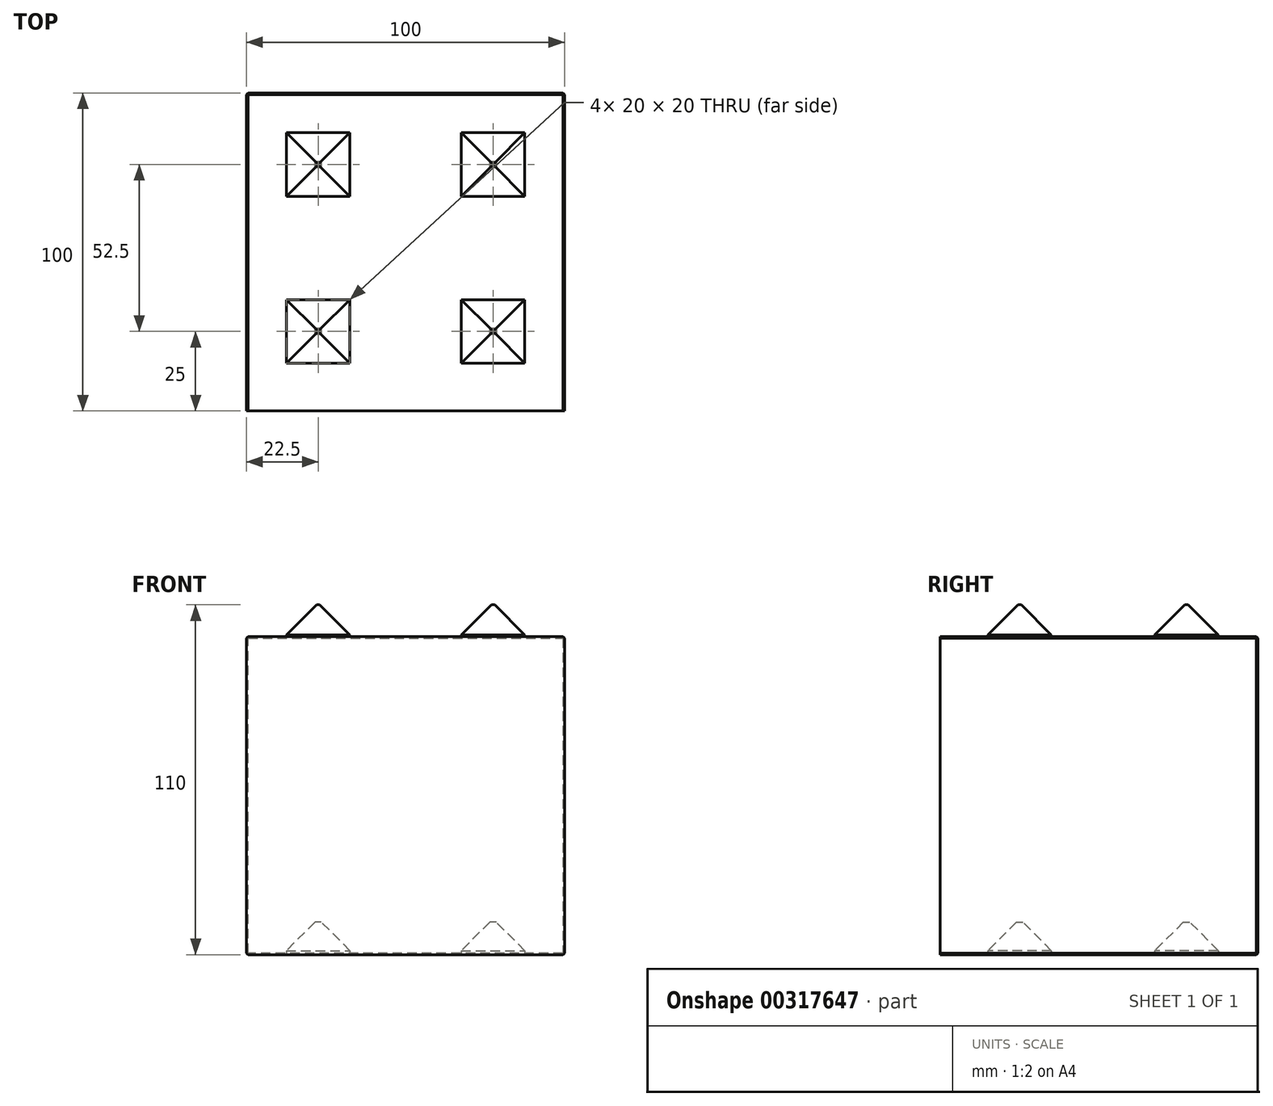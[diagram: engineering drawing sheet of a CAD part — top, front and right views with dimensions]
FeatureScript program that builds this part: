
annotation { "Feature Type Name" : "Feature", "Feature Type Description" : "" }
export const myFeature = defineFeature(function(context is Context, id is Id, definition is map)
    precondition{}
    {
        {
            var Q0;
            Q0=qCreatedBy(makeId("Front.planeOp"),FACE);
            var sketch = newSketch(context, id + "F0", { "sketchPlane" : qUnion([Q0])});
            skLineSegment(sketch, "E0.bottom", {"start": v(-50, 50) * mm, "end": v(50, 50) * mm});
            skLineSegment(sketch, "E0.top", {"start": v(-50, -50) * mm, "end": v(50, -50) * mm});
            skLineSegment(sketch, "E0.left", {"start": v(-50, 50) * mm, "end": v(-50, -50) * mm});
            skLineSegment(sketch, "E0.right", {"start": v(50, 50) * mm, "end": v(50, -50) * mm});
            skSolve(sketch);
        }
        {
            var Q0;
            Q0 = qSketchRegion(id + "F0", true);
            extrude(context, id + "F1", {"entities" : qUnion([Q0]), "endBound" : BoundingType.SYMMETRIC, "depth" : 200 * mm});
        }
        {
            var Q0;
            Q0=makeQuery(id+"F1.opExtrude","SWEPT_FACE",FACE,{"disambiguationData":[OSD([sQuery(id+"F0.wireOp",EDGE,"E0.bottom")])]});
            var sketch = newSketch(context, id + "F2", { "sketchPlane" : qUnion([Q0])});
            skLineSegment(sketch, "E1", {"start": v(-37.5, 87.5) * mm, "end": v(-37.5, 67.5) * mm});
            skLineSegment(sketch, "E2", {"start": v(-17.5, 87.5) * mm, "end": v(-17.5, 67.5) * mm});
            skLineSegment(sketch, "E3", {"start": v(17.5, 87.5) * mm, "end": v(17.5, 67.5) * mm});
            skLineSegment(sketch, "E4", {"start": v(37.5, 87.5) * mm, "end": v(37.5, 67.5) * mm});
            skLineSegment(sketch, "E5", {"start": v(-37.5, 87.5) * mm, "end": v(-17.5, 87.5) * mm});
            skLineSegment(sketch, "E6", {"start": v(-37.5, 67.5) * mm, "end": v(-17.5, 67.5) * mm});
            skLineSegment(sketch, "E7", {"start": v(-37.5, 35) * mm, "end": v(-17.5, 35) * mm});
            skLineSegment(sketch, "E8", {"start": v(-37.5, 15) * mm, "end": v(-17.5, 15) * mm});
            skLineSegment(sketch, "E9", {"start": v(-37.5, -15) * mm, "end": v(-17.5, -15) * mm});
            skLineSegment(sketch, "E10", {"start": v(-37.5, -35) * mm, "end": v(-17.5, -35) * mm});
            skLineSegment(sketch, "E11", {"start": v(-37.5, -67.5) * mm, "end": v(-17.5, -67.5) * mm});
            skLineSegment(sketch, "E12", {"start": v(-37.5, -87.5) * mm, "end": v(-17.5, -87.5) * mm});
            skLineSegment(sketch, "E13.trimOffspring", {"start": v(-37.5, -67.5) * mm, "end": v(-37.5, -87.5) * mm});
            skLineSegment(sketch, "E14.trimOffspring", {"start": v(-17.5, -67.5) * mm, "end": v(-17.5, -87.5) * mm});
            skLineSegment(sketch, "E15.trimOffspring", {"start": v(17.5, -67.5) * mm, "end": v(17.5, -87.5) * mm});
            skLineSegment(sketch, "E16.trimOffspring", {"start": v(37.5, -67.5) * mm, "end": v(37.5, -87.5) * mm});
            skLineSegment(sketch, "E17.trimOffspring", {"start": v(17.5, -67.5) * mm, "end": v(37.5, -67.5) * mm});
            skLineSegment(sketch, "E18.trimOffspring", {"start": v(17.5, -87.5) * mm, "end": v(37.5, -87.5) * mm});
            skLineSegment(sketch, "E19.trimOffspring", {"start": v(17.5, -15) * mm, "end": v(37.5, -15) * mm});
            skLineSegment(sketch, "E20.trimOffspring", {"start": v(17.5, -35) * mm, "end": v(37.5, -35) * mm});
            skLineSegment(sketch, "E21.trimOffspring", {"start": v(17.5, 15) * mm, "end": v(37.5, 15) * mm});
            skLineSegment(sketch, "E22.trimOffspring", {"start": v(17.5, 35) * mm, "end": v(37.5, 35) * mm});
            skLineSegment(sketch, "E23.trimOffspring", {"start": v(17.5, 67.5) * mm, "end": v(37.5, 67.5) * mm});
            skLineSegment(sketch, "E24.trimOffspring", {"start": v(17.5, 87.5) * mm, "end": v(37.5, 87.5) * mm});
            skLineSegment(sketch, "E25.trimOffspring", {"start": v(-37.5, 35) * mm, "end": v(-37.5, 15) * mm});
            skLineSegment(sketch, "E26.trimOffspring", {"start": v(-17.5, 35) * mm, "end": v(-17.5, 15) * mm});
            skLineSegment(sketch, "E27.trimOffspring", {"start": v(17.5, 35) * mm, "end": v(17.5, 15) * mm});
            skLineSegment(sketch, "E28.trimOffspring", {"start": v(37.5, 35) * mm, "end": v(37.5, 15) * mm});
            skLineSegment(sketch, "E29.trimOffspring", {"start": v(-37.5, -15) * mm, "end": v(-37.5, -35) * mm});
            skLineSegment(sketch, "E30.trimOffspring", {"start": v(-17.5, -15) * mm, "end": v(-17.5, -35) * mm});
            skLineSegment(sketch, "E31.trimOffspring", {"start": v(17.5, -15) * mm, "end": v(17.5, -35) * mm});
            skLineSegment(sketch, "E32.trimOffspring", {"start": v(37.5, -15) * mm, "end": v(37.5, -35) * mm});
            skSolve(sketch);
        }
        {
            var Q0;
            Q0 = qSketchRegion(id + "F2", true);
            extrude(context, id + "F3", {"entities" : qUnion([Q0]), "operationType" : NewBodyOperationType.ADD, "depth" : 10 * mm});
        }
        {
            var Q0;
            Q0=makeQuery(id+"F3.opExtrude","CAP_FACE",FACE,{"disambiguationData":[OSD([sQuery(id+"F2.wireOp",EDGE,"E15.trimOffspring"),sQuery(id+"F2.wireOp",EDGE,"E16.trimOffspring"),sQuery(id+"F2.wireOp",EDGE,"E17.trimOffspring"),sQuery(id+"F2.wireOp",EDGE,"E18.trimOffspring")])],"isStart":false});
            var Q1;
            Q1=makeQuery(id+"F3.opExtrude","CAP_FACE",FACE,{"disambiguationData":[OSD([sQuery(id+"F2.wireOp",EDGE,"E19.trimOffspring"),sQuery(id+"F2.wireOp",EDGE,"E20.trimOffspring"),sQuery(id+"F2.wireOp",EDGE,"E31.trimOffspring"),sQuery(id+"F2.wireOp",EDGE,"E32.trimOffspring")])],"isStart":false});
            var Q2;
            Q2=makeQuery(id+"F3.opExtrude","CAP_FACE",FACE,{"disambiguationData":[OSD([sQuery(id+"F2.wireOp",EDGE,"E11"),sQuery(id+"F2.wireOp",EDGE,"E12"),sQuery(id+"F2.wireOp",EDGE,"E13.trimOffspring"),sQuery(id+"F2.wireOp",EDGE,"E14.trimOffspring")])],"isStart":false});
            var Q3;
            Q3=makeQuery(id+"F3.opExtrude","CAP_FACE",FACE,{"disambiguationData":[OSD([sQuery(id+"F2.wireOp",EDGE,"E9"),sQuery(id+"F2.wireOp",EDGE,"E10"),sQuery(id+"F2.wireOp",EDGE,"E29.trimOffspring"),sQuery(id+"F2.wireOp",EDGE,"E30.trimOffspring")])],"isStart":false});
            var Q4;
            Q4=makeQuery(id+"F3.opExtrude","CAP_FACE",FACE,{"disambiguationData":[OSD([sQuery(id+"F2.wireOp",EDGE,"E7"),sQuery(id+"F2.wireOp",EDGE,"E8"),sQuery(id+"F2.wireOp",EDGE,"E25.trimOffspring"),sQuery(id+"F2.wireOp",EDGE,"E26.trimOffspring")])],"isStart":false});
            var Q5;
            Q5=makeQuery(id+"F3.opExtrude","CAP_FACE",FACE,{"disambiguationData":[OSD([sQuery(id+"F2.wireOp",EDGE,"E1"),sQuery(id+"F2.wireOp",EDGE,"E2"),sQuery(id+"F2.wireOp",EDGE,"E5"),sQuery(id+"F2.wireOp",EDGE,"E6")])],"isStart":false});
            var Q6;
            Q6=makeQuery(id+"F3.opExtrude","CAP_FACE",FACE,{"disambiguationData":[OSD([sQuery(id+"F2.wireOp",EDGE,"E3"),sQuery(id+"F2.wireOp",EDGE,"E4"),sQuery(id+"F2.wireOp",EDGE,"E23.trimOffspring"),sQuery(id+"F2.wireOp",EDGE,"E24.trimOffspring")])],"isStart":false});
            var Q7;
            Q7=makeQuery(id+"F3.opExtrude","CAP_FACE",FACE,{"disambiguationData":[OSD([sQuery(id+"F2.wireOp",EDGE,"E21.trimOffspring"),sQuery(id+"F2.wireOp",EDGE,"E22.trimOffspring"),sQuery(id+"F2.wireOp",EDGE,"E27.trimOffspring"),sQuery(id+"F2.wireOp",EDGE,"E28.trimOffspring")])],"isStart":false});
            chamfer(context, id + "F4", {"entities" : qUnion([Q0, Q1, Q2, Q3, Q4, Q5, Q6, Q7]), "width" : 9.5 * mm, "tangentPropagation" : true});
        }
        {
            var Q0;
            Q0=makeQuery(id+"F1.opExtrude","SWEPT_FACE",FACE,{"disambiguationData":[OSD([sQuery(id+"F0.wireOp",EDGE,"E0.top")])]});
            var sketch = newSketch(context, id + "F5", { "sketchPlane" : qUnion([Q0])});
            skLineSegment(sketch, "E33", {"start": v(-37.5, 87.5) * mm, "end": v(-37.5, 67.5) * mm});
            skLineSegment(sketch, "E34", {"start": v(-17.5, 87.5) * mm, "end": v(-17.5, 67.5) * mm});
            skLineSegment(sketch, "E35", {"start": v(17.5, 87.5) * mm, "end": v(17.5, 67.5) * mm});
            skLineSegment(sketch, "E36", {"start": v(37.5, 87.5) * mm, "end": v(37.5, 67.5) * mm});
            skLineSegment(sketch, "E37", {"start": v(-37.5, 87.5) * mm, "end": v(-17.5, 87.5) * mm});
            skLineSegment(sketch, "E38", {"start": v(-37.5, 67.5) * mm, "end": v(-17.5, 67.5) * mm});
            skLineSegment(sketch, "E39", {"start": v(-37.5, 35) * mm, "end": v(-17.5, 35) * mm});
            skLineSegment(sketch, "E40", {"start": v(-37.5, 15) * mm, "end": v(-17.5, 15) * mm});
            skLineSegment(sketch, "E41", {"start": v(-37.5, -15) * mm, "end": v(-17.5, -15) * mm});
            skLineSegment(sketch, "E42", {"start": v(-37.5, -35) * mm, "end": v(-17.5, -35) * mm});
            skLineSegment(sketch, "E43", {"start": v(-37.5, -67.5) * mm, "end": v(-17.5, -67.5) * mm});
            skLineSegment(sketch, "E44", {"start": v(-37.5, -87.5) * mm, "end": v(-17.5, -87.5) * mm});
            skLineSegment(sketch, "E45.trimOffspring", {"start": v(-37.5, -67.5) * mm, "end": v(-37.5, -87.5) * mm});
            skLineSegment(sketch, "E46.trimOffspring", {"start": v(-17.5, -67.5) * mm, "end": v(-17.5, -87.5) * mm});
            skLineSegment(sketch, "E47.trimOffspring", {"start": v(17.5, -67.5) * mm, "end": v(17.5, -87.5) * mm});
            skLineSegment(sketch, "E48.trimOffspring", {"start": v(37.5, -67.5) * mm, "end": v(37.5, -87.5) * mm});
            skLineSegment(sketch, "E49.trimOffspring", {"start": v(17.5, -67.5) * mm, "end": v(37.5, -67.5) * mm});
            skLineSegment(sketch, "E50.trimOffspring", {"start": v(17.5, -87.5) * mm, "end": v(37.5, -87.5) * mm});
            skLineSegment(sketch, "E51.trimOffspring", {"start": v(17.5, -15) * mm, "end": v(37.5, -15) * mm});
            skLineSegment(sketch, "E52.trimOffspring", {"start": v(17.5, -35) * mm, "end": v(37.5, -35) * mm});
            skLineSegment(sketch, "E53.trimOffspring", {"start": v(17.5, 15) * mm, "end": v(37.5, 15) * mm});
            skLineSegment(sketch, "E54.trimOffspring", {"start": v(17.5, 35) * mm, "end": v(37.5, 35) * mm});
            skLineSegment(sketch, "E55.trimOffspring", {"start": v(17.5, 67.5) * mm, "end": v(37.5, 67.5) * mm});
            skLineSegment(sketch, "E56.trimOffspring", {"start": v(17.5, 87.5) * mm, "end": v(37.5, 87.5) * mm});
            skLineSegment(sketch, "E57.trimOffspring", {"start": v(-37.5, 35) * mm, "end": v(-37.5, 15) * mm});
            skLineSegment(sketch, "E58.trimOffspring", {"start": v(-17.5, 35) * mm, "end": v(-17.5, 15) * mm});
            skLineSegment(sketch, "E59.trimOffspring", {"start": v(17.5, 35) * mm, "end": v(17.5, 15) * mm});
            skLineSegment(sketch, "E60.trimOffspring", {"start": v(37.5, 35) * mm, "end": v(37.5, 15) * mm});
            skLineSegment(sketch, "E61.trimOffspring", {"start": v(-37.5, -15) * mm, "end": v(-37.5, -35) * mm});
            skLineSegment(sketch, "E62.trimOffspring", {"start": v(-17.5, -15) * mm, "end": v(-17.5, -35) * mm});
            skLineSegment(sketch, "E63.trimOffspring", {"start": v(17.5, -15) * mm, "end": v(17.5, -35) * mm});
            skLineSegment(sketch, "E64.trimOffspring", {"start": v(37.5, -15) * mm, "end": v(37.5, -35) * mm});
            skSolve(sketch);
        }
        {
            var Q0;
            Q0=makeQuery(id+"F5.imprint","IMPRINT",FACE,{"disambiguationData":[TD([[makeQuery(id+"F5.imprint","IMPRINT",EDGE,{"derivedFrom":sQuery(id+"F5.wireOp",EDGE,"E33")}),1.0]])]});
            var Q1;
            Q1=makeQuery(id+"F5.imprint","IMPRINT",FACE,{"disambiguationData":[TD([[makeQuery(id+"F5.imprint","IMPRINT",EDGE,{"derivedFrom":sQuery(id+"F5.wireOp",EDGE,"E35")}),1.0]])]});
            var Q2;
            Q2=makeQuery(id+"F5.imprint","IMPRINT",FACE,{"disambiguationData":[TD([[makeQuery(id+"F5.imprint","IMPRINT",EDGE,{"derivedFrom":sQuery(id+"F5.wireOp",EDGE,"E53.trimOffspring")}),1.0]])]});
            var Q3;
            Q3=makeQuery(id+"F5.imprint","IMPRINT",FACE,{"disambiguationData":[TD([[makeQuery(id+"F5.imprint","IMPRINT",EDGE,{"derivedFrom":sQuery(id+"F5.wireOp",EDGE,"E39")}),-1.0]])]});
            var Q4;
            Q4=makeQuery(id+"F5.imprint","IMPRINT",FACE,{"disambiguationData":[TD([[makeQuery(id+"F5.imprint","IMPRINT",EDGE,{"derivedFrom":sQuery(id+"F5.wireOp",EDGE,"E41")}),-1.0]])]});
            var Q5;
            Q5=makeQuery(id+"F5.imprint","IMPRINT",FACE,{"disambiguationData":[TD([[makeQuery(id+"F5.imprint","IMPRINT",EDGE,{"derivedFrom":sQuery(id+"F5.wireOp",EDGE,"E51.trimOffspring")}),-1.0]])]});
            var Q6;
            Q6=makeQuery(id+"F5.imprint","IMPRINT",FACE,{"disambiguationData":[TD([[makeQuery(id+"F5.imprint","IMPRINT",EDGE,{"derivedFrom":sQuery(id+"F5.wireOp",EDGE,"E47.trimOffspring")}),1.0]])]});
            var Q7;
            Q7=makeQuery(id+"F5.imprint","IMPRINT",FACE,{"disambiguationData":[TD([[makeQuery(id+"F5.imprint","IMPRINT",EDGE,{"derivedFrom":sQuery(id+"F5.wireOp",EDGE,"E43")}),-1.0]])]});
            extrude(context, id + "F6", {"entities" : qUnion([Q0, Q1, Q2, Q3, Q4, Q5, Q6, Q7]), "operationType" : NewBodyOperationType.REMOVE, "oppositeDirection" : true, "depth" : 10.25 * mm});
        }
        {
            var Q0;
            Q0=makeQuery(id+"F6.boolean.opBoolean","COPY",FACE,{"derivedFrom":makeQuery(id+"F6.opExtrude","CAP_FACE",FACE,{"disambiguationData":[OSD([sQuery(id+"F5.wireOp",EDGE,"E35"),sQuery(id+"F5.wireOp",EDGE,"E36"),sQuery(id+"F5.wireOp",EDGE,"E55.trimOffspring"),sQuery(id+"F5.wireOp",EDGE,"E56.trimOffspring")])],"isStart":false})});
            var Q1;
            Q1=makeQuery(id+"F6.boolean.opBoolean","COPY",FACE,{"derivedFrom":makeQuery(id+"F6.opExtrude","CAP_FACE",FACE,{"disambiguationData":[OSD([sQuery(id+"F5.wireOp",EDGE,"E33"),sQuery(id+"F5.wireOp",EDGE,"E34"),sQuery(id+"F5.wireOp",EDGE,"E37"),sQuery(id+"F5.wireOp",EDGE,"E38")])],"isStart":false})});
            var Q2;
            Q2=makeQuery(id+"F6.boolean.opBoolean","COPY",FACE,{"derivedFrom":makeQuery(id+"F6.opExtrude","CAP_FACE",FACE,{"disambiguationData":[OSD([sQuery(id+"F5.wireOp",EDGE,"E39"),sQuery(id+"F5.wireOp",EDGE,"E40"),sQuery(id+"F5.wireOp",EDGE,"E57.trimOffspring"),sQuery(id+"F5.wireOp",EDGE,"E58.trimOffspring")])],"isStart":false})});
            var Q3;
            Q3=makeQuery(id+"F6.boolean.opBoolean","COPY",FACE,{"derivedFrom":makeQuery(id+"F6.opExtrude","CAP_FACE",FACE,{"disambiguationData":[OSD([sQuery(id+"F5.wireOp",EDGE,"E53.trimOffspring"),sQuery(id+"F5.wireOp",EDGE,"E54.trimOffspring"),sQuery(id+"F5.wireOp",EDGE,"E59.trimOffspring"),sQuery(id+"F5.wireOp",EDGE,"E60.trimOffspring")])],"isStart":false})});
            var Q4;
            Q4=makeQuery(id+"F6.boolean.opBoolean","COPY",FACE,{"derivedFrom":makeQuery(id+"F6.opExtrude","CAP_FACE",FACE,{"disambiguationData":[OSD([sQuery(id+"F5.wireOp",EDGE,"E51.trimOffspring"),sQuery(id+"F5.wireOp",EDGE,"E52.trimOffspring"),sQuery(id+"F5.wireOp",EDGE,"E63.trimOffspring"),sQuery(id+"F5.wireOp",EDGE,"E64.trimOffspring")])],"isStart":false})});
            var Q5;
            Q5=makeQuery(id+"F6.boolean.opBoolean","COPY",FACE,{"derivedFrom":makeQuery(id+"F6.opExtrude","CAP_FACE",FACE,{"disambiguationData":[OSD([sQuery(id+"F5.wireOp",EDGE,"E41"),sQuery(id+"F5.wireOp",EDGE,"E42"),sQuery(id+"F5.wireOp",EDGE,"E61.trimOffspring"),sQuery(id+"F5.wireOp",EDGE,"E62.trimOffspring")])],"isStart":false})});
            var Q6;
            Q6=makeQuery(id+"F6.boolean.opBoolean","COPY",FACE,{"derivedFrom":makeQuery(id+"F6.opExtrude","CAP_FACE",FACE,{"disambiguationData":[OSD([sQuery(id+"F5.wireOp",EDGE,"E43"),sQuery(id+"F5.wireOp",EDGE,"E44"),sQuery(id+"F5.wireOp",EDGE,"E45.trimOffspring"),sQuery(id+"F5.wireOp",EDGE,"E46.trimOffspring")])],"isStart":false})});
            var Q7;
            Q7=makeQuery(id+"F6.boolean.opBoolean","COPY",FACE,{"derivedFrom":makeQuery(id+"F6.opExtrude","CAP_FACE",FACE,{"disambiguationData":[OSD([sQuery(id+"F5.wireOp",EDGE,"E47.trimOffspring"),sQuery(id+"F5.wireOp",EDGE,"E48.trimOffspring"),sQuery(id+"F5.wireOp",EDGE,"E49.trimOffspring"),sQuery(id+"F5.wireOp",EDGE,"E50.trimOffspring")])],"isStart":false})});
            chamfer(context, id + "F7", {"entities" : qUnion([Q0, Q1, Q2, Q3, Q4, Q5, Q6, Q7]), "width" : 9 * mm, "tangentPropagation" : true});
        }
        {
            var Q0;
            Q0=makeQuery(id+"F1.opExtrude","CAP_FACE",FACE,{"disambiguationData":[OSD([sQuery(id+"F0.wireOp",EDGE,"E0.bottom"),sQuery(id+"F0.wireOp",EDGE,"E0.top"),sQuery(id+"F0.wireOp",EDGE,"E0.left"),sQuery(id+"F0.wireOp",EDGE,"E0.right")])],"isStart":false});
            var Q1;
            Q1=makeQuery(id+"F1.opExtrude","CAP_FACE",FACE,{"disambiguationData":[OSD([sQuery(id+"F0.wireOp",EDGE,"E0.bottom"),sQuery(id+"F0.wireOp",EDGE,"E0.top"),sQuery(id+"F0.wireOp",EDGE,"E0.left"),sQuery(id+"F0.wireOp",EDGE,"E0.right")])],"isStart":true});
            var Q2;
            Q2=makeQuery(id+"F1.opExtrude","SWEPT_FACE",FACE,{"disambiguationData":[OSD([sQuery(id+"F0.wireOp",EDGE,"E0.right")])]});
            var Q3;
            Q3=makeQuery(id+"F1.opExtrude","SWEPT_FACE",FACE,{"disambiguationData":[OSD([sQuery(id+"F0.wireOp",EDGE,"E0.left")])]});
            chamfer(context, id + "F8", {"entities" : qUnion([Q0, Q1, Q2, Q3]), "width" : .5 * mm, "tangentPropagation" : true});
        }
        {
            var Q0;
            Q0=makeQuery(id+"F1.opExtrude","SWEPT_FACE",FACE,{"disambiguationData":[OSD([sQuery(id+"F0.wireOp",EDGE,"E0.right")])]});
            var sketch = newSketch(context, id + "F9", { "sketchPlane" : qUnion([Q0])});
            skLineSegment(sketch, "E65", {"start": v(0, 0) * mm, "end": v(0, 74.22) * mm});
            skPoint(sketch, "E65.endSnap0", {"position": v(0, 49.5) * mm});
            skLineSegment(sketch, "E66", {"start": v(0, 74.22) * mm, "end": v(-106.33, 74.22) * mm});
            skLineSegment(sketch, "E67", {"start": v(-106.33, 74.22) * mm, "end": v(-106.33, -62.88) * mm});
            skLineSegment(sketch, "E68", {"start": v(-106.33, -62.88) * mm, "end": v(0, -62.88) * mm});
            skLineSegment(sketch, "E69", {"start": v(0, -62.88) * mm, "end": v(0, 0) * mm});
            skSolve(sketch);
        }
        {
            var Q0;
            Q0 = qSketchRegion(id + "F9", true);
            extrude(context, id + "F10", {"entities" : qUnion([Q0]), "operationType" : NewBodyOperationType.REMOVE, "oppositeDirection" : true, "depth" : 100 * mm});
        }
    });
